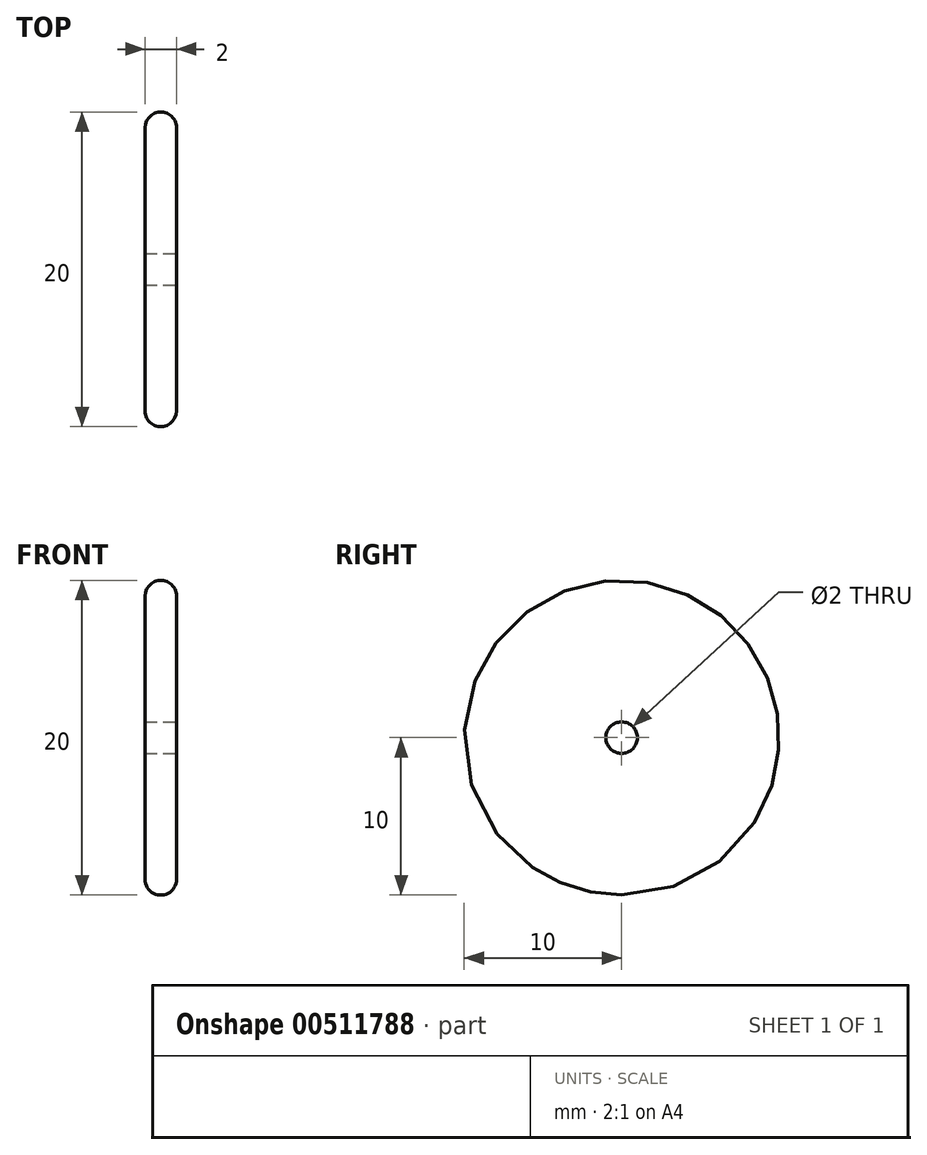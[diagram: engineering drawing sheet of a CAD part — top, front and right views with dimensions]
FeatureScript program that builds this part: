
annotation { "Feature Type Name" : "Feature", "Feature Type Description" : "" }
export const myFeature = defineFeature(function(context is Context, id is Id, definition is map)
    precondition{}
    {
        {
            var Q0;
            Q0=qCreatedBy(makeId("Right.planeOp"),FACE);
            var sketch = newSketch(context, id + "F0", { "sketchPlane" : qUnion([Q0])});
            skCircle(sketch, "E0", {"center": v(0, 0) * mm, "radius": 10 * mm});
            skSolve(sketch);
        }
        {
            var Q0;
            Q0 = qSketchRegion(id + "F0", true);
            extrude(context, id + "F1", {"entities" : qUnion([Q0]), "depth" : 2 * mm});
        }
        {
            var Q0;
            Q0=makeQuery(id+"F1.opExtrude","SWEPT_FACE",FACE,{"disambiguationData":[OSD([sQuery(id+"F0.wireOp",EDGE,"E0")])]});
            fillet(context, id + "F2", {"entities" : qUnion([Q0]), "radius" : 1 * mm, "tangentPropagation" : true, "allowEdgeOverflow" : false});
        }
        {
            var Q0;
            Q0=makeQuery(id+"F1.opExtrude","CAP_FACE",FACE,{"disambiguationData":[OSD([sQuery(id+"F0.wireOp",EDGE,"E0")])],"isStart":false});
            var sketch = newSketch(context, id + "F3", { "sketchPlane" : qUnion([Q0])});
            skCircle(sketch, "E1", {"center": v(0, 0) * mm, "radius": 1 * mm});
            skSolve(sketch);
        }
        {
            var Q0;
            Q0=sQuery(id+"F3.wireOp",VERTEX,"E1.center");
            var Q1;
            Q1=makeQuery(id+"F1.opExtrude","SWEPT_BODY",BODY,{"disambiguationData":[OSD([sQuery(id+"F0.wireOp",EDGE,"E0")])]});
            hole(context, id + "F4", {"style" : HoleStyle.SIMPLE, "endStyle" : HoleEndStyle.THROUGH, "holeDiameter" : 2 * mm, "isTappedThrough" : true, "tappedDepth" : 12 * mm, "tapClearance" : 3, "locations" : qUnion([Q0]), "scope" : qUnion([Q1])});
        }
    });
